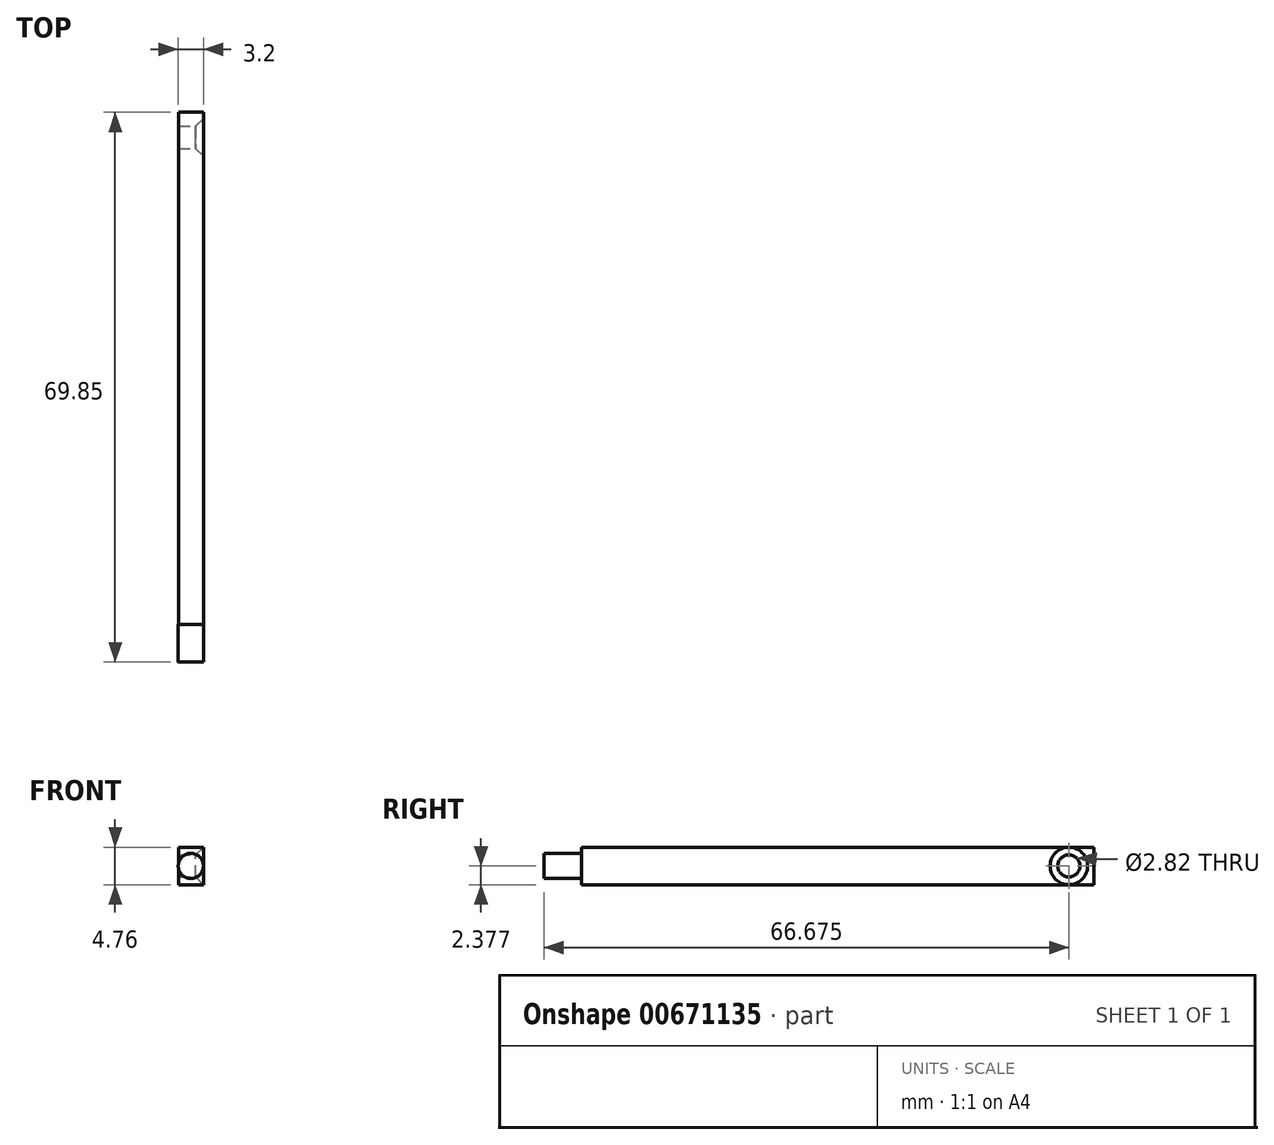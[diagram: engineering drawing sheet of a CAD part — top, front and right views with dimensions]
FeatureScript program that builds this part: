
annotation { "Feature Type Name" : "Feature", "Feature Type Description" : "" }
export const myFeature = defineFeature(function(context is Context, id is Id, definition is map)
    precondition{}
    {
        {
            var Q0;
            Q0=qCreatedBy(makeId("Front.planeOp"),FACE);
            var sketch = newSketch(context, id + "F0", { "sketchPlane" : qUnion([Q0])});
            skLineSegment(sketch, "E0.bottom", {"start": v(23.62, 20.3) * mm, "end": v(26.8, 20.3) * mm});
            skLineSegment(sketch, "E0.top", {"start": v(23.62, 15.54) * mm, "end": v(26.8, 15.54) * mm});
            skLineSegment(sketch, "E0.left", {"start": v(23.62, 20.3) * mm, "end": v(23.62, 15.54) * mm});
            skLineSegment(sketch, "E0.right", {"start": v(26.8, 20.3) * mm, "end": v(26.8, 15.54) * mm});
            skSolve(sketch);
        }
        {
            var Q0;
            Q0=qSketchRegion(id+"F0",true);
            extrude(context, id + "F1", {"entities" : qUnion([Q0]), "depth" : 65.1 * mm});
        }
        {
            var Q0;
            Q0=makeQuery(id+"F1.opExtrude","CAP_FACE",FACE,{"disambiguationData":[OSD([sQuery(id+"F0.wireOp",EDGE,"E0.bottom"),sQuery(id+"F0.wireOp",EDGE,"E0.top"),sQuery(id+"F0.wireOp",EDGE,"E0.left"),sQuery(id+"F0.wireOp",EDGE,"E0.right")])],"isStart":false});
            var sketch = newSketch(context, id + "F2", { "sketchPlane" : qUnion([Q0])});
            skCircle(sketch, "E1", {"center": v(25.21, 17.92) * mm, "radius": 1.6 * mm});
            skSolve(sketch);
        }
        {
            var Q0;
            Q0=qSketchRegion(id+"F2",true);
            extrude(context, id + "F3", {"entities" : qUnion([Q0]), "operationType" : NewBodyOperationType.ADD, "depth" : 4.76 * mm});
        }
        {
            var Q0;
            Q0=makeQuery(id+"F1.opExtrude","SWEPT_FACE",FACE,{"disambiguationData":[OSD([sQuery(id+"F0.wireOp",EDGE,"E0.right")])]});
            var sketch = newSketch(context, id + "F4", { "sketchPlane" : qUnion([Q0])});
            skPoint(sketch, "E2", {"position": v(-3.18, 17.92) * mm});
            skSolve(sketch);
        }
        {
            var Q0;
            Q0=sQuery(id+"F4.wireOp",VERTEX,"E2");
            var Q1;
            Q1=makeQuery(id+"F1.opExtrude","SWEPT_BODY",BODY,{"disambiguationData":[OSD([sQuery(id+"F0.wireOp",EDGE,"E0.bottom"),sQuery(id+"F0.wireOp",EDGE,"E0.top"),sQuery(id+"F0.wireOp",EDGE,"E0.left"),sQuery(id+"F0.wireOp",EDGE,"E0.right")])]});
            hole(context, id + "F5", {"style" : HoleStyle.C_SINK, "endStyle" : HoleEndStyle.THROUGH, "holeDiameter" : 2.82 * mm, "cSinkDiameter" : 4.76 * mm, "cSinkAngle" : 90 * degree, "tappedDepth" : 12.7 * mm, "tapClearance" : 3, "locations" : qUnion([Q0]), "scope" : qUnion([Q1])});
        }
    });
